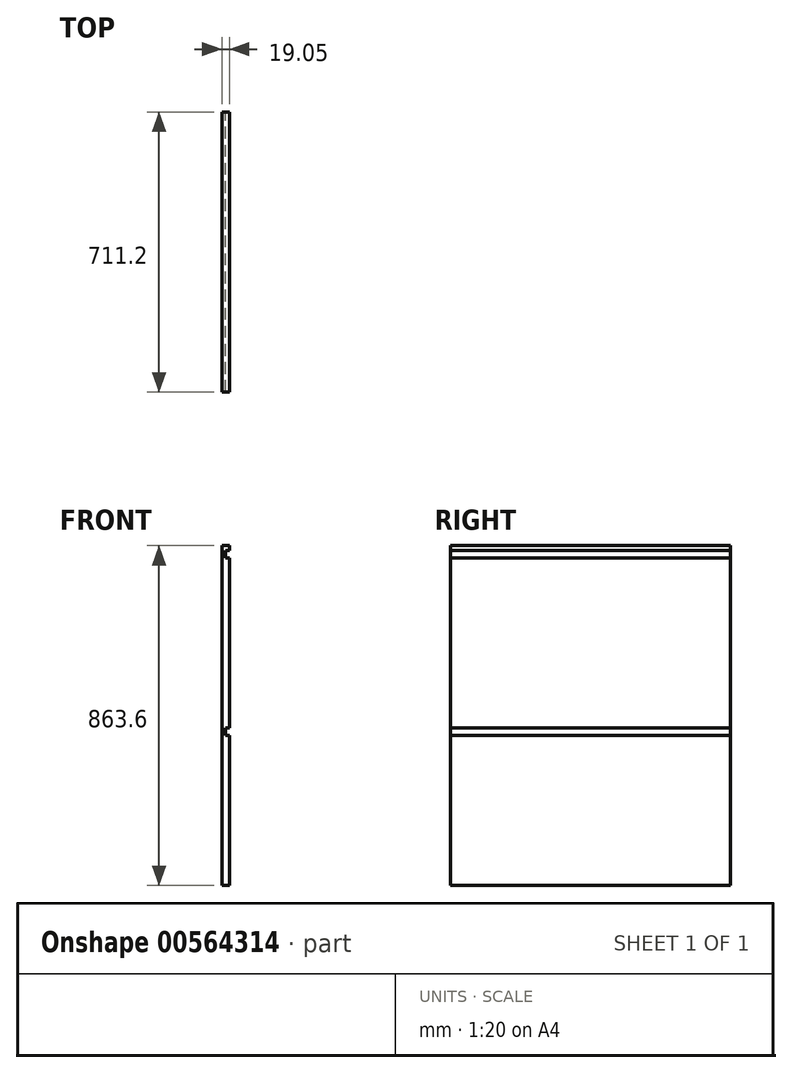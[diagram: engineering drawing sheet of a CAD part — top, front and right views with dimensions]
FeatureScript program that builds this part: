
annotation { "Feature Type Name" : "Feature", "Feature Type Description" : "" }
export const myFeature = defineFeature(function(context is Context, id is Id, definition is map)
    precondition{}
    {
        {
            var Q0;
            Q0=qCreatedBy(makeId("Front.planeOp"),FACE);
            var sketch = newSketch(context, id + "F0", { "sketchPlane" : qUnion([Q0])});
            skLineSegment(sketch, "E0.bottom", {"start": v(-323.85, 434.24) * mm, "end": v(-304.8, 434.24) * mm});
            skLineSegment(sketch, "E0.top", {"start": v(-323.85, -429.36) * mm, "end": v(-304.8, -429.36) * mm});
            skLineSegment(sketch, "E0.left", {"start": v(-323.85, 434.24) * mm, "end": v(-323.85, -429.36) * mm});
            skLineSegment(sketch, "E0.right", {"start": v(-304.8, 434.24) * mm, "end": v(-304.8, 421.54) * mm});
            skLineSegment(sketch, "E1.bottom", {"start": v(-304.8, 421.54) * mm, "end": v(-314.33, 421.54) * mm});
            skLineSegment(sketch, "E1.top", {"start": v(-304.8, 402.49) * mm, "end": v(-314.33, 402.49) * mm});
            skLineSegment(sketch, "E1.right", {"start": v(-314.33, 421.54) * mm, "end": v(-314.33, 402.49) * mm});
            skLineSegment(sketch, "E2.trimOffspring", {"start": v(-304.8, 402.49) * mm, "end": v(-304.8, -29.31) * mm});
            skLineSegment(sketch, "E3.bottom", {"start": v(-304.8, -29.31) * mm, "end": v(-314.33, -29.31) * mm});
            skLineSegment(sketch, "E3.top", {"start": v(-304.8, -48.36) * mm, "end": v(-314.33, -48.36) * mm});
            skLineSegment(sketch, "E3.right", {"start": v(-314.33, -29.31) * mm, "end": v(-314.33, -48.36) * mm});
            skLineSegment(sketch, "E4.trimOffspring", {"start": v(-304.8, -48.36) * mm, "end": v(-304.8, -429.36) * mm});
            skSolve(sketch);
        }
        {
            var Q0;
            Q0 = qSketchRegion(id + "F0", true);
            extrude(context, id + "F1", {"entities" : qUnion([Q0]), "depth" : 711.2 * mm, "offsetDistance" : 25.4 * mm});
        }
    });
